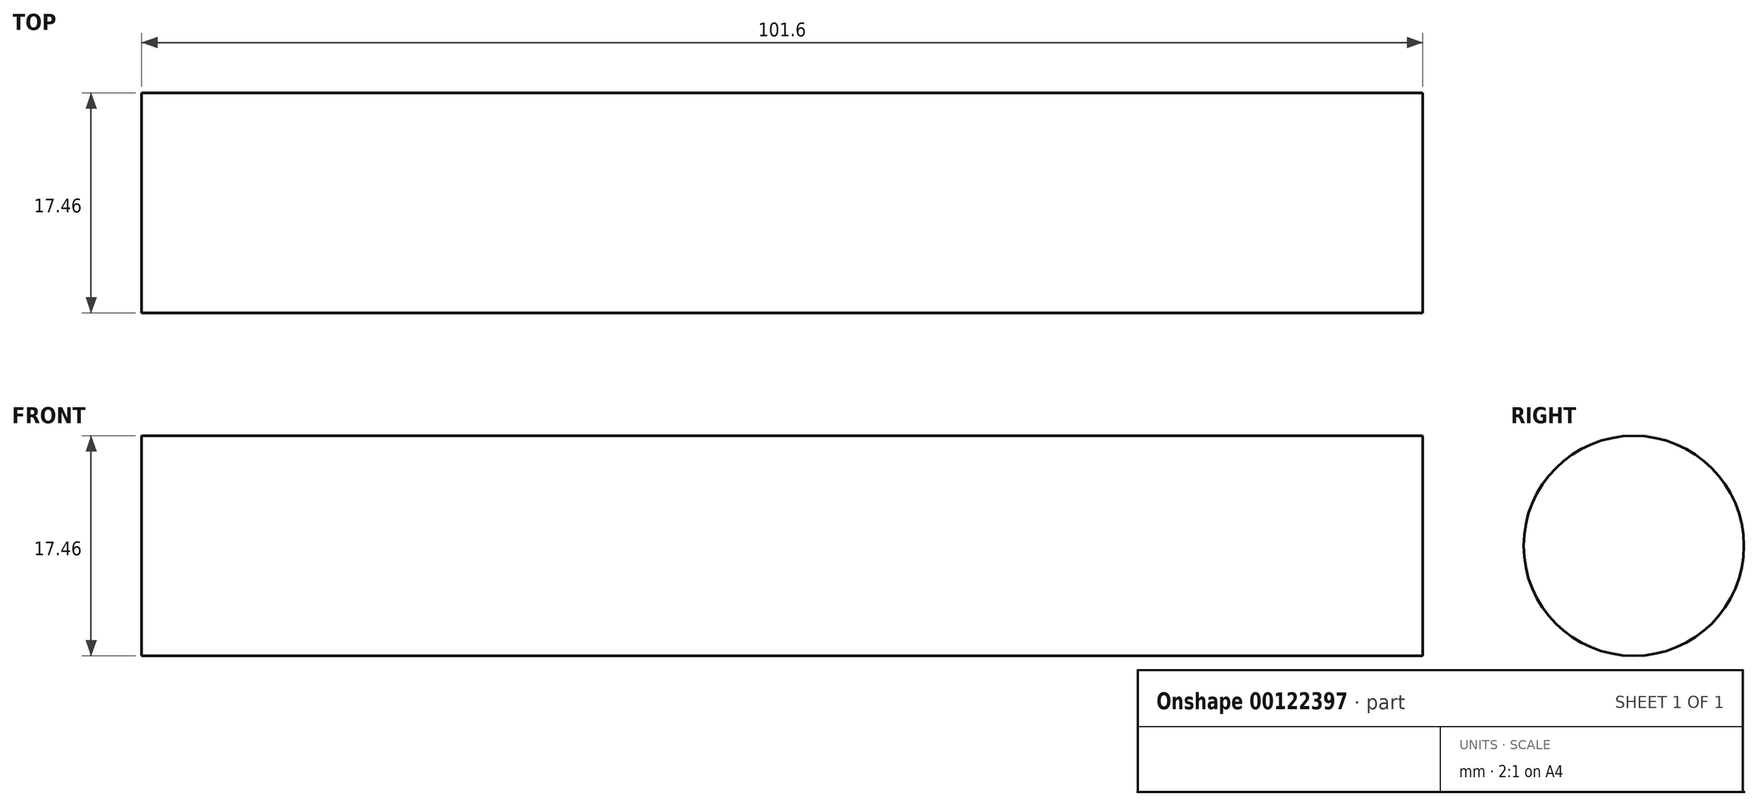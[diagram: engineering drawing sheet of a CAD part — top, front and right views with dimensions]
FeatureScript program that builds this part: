
annotation { "Feature Type Name" : "Feature", "Feature Type Description" : "" }
export const myFeature = defineFeature(function(context is Context, id is Id, definition is map)
    precondition{}
    {
        {
            var Q0;
            Q0=qCreatedBy(makeId("Right.planeOp"),FACE);
            var sketch = newSketch(context, id + "F0", { "sketchPlane" : qUnion([Q0])});
            skCircle(sketch, "E0", {"center": v(0, 0) * mm, "radius": 8.73 * mm});
            skSolve(sketch);
        }
        {
            var Q0;
            Q0=makeQuery(id+"F0.imprint","IMPRINT",FACE,{"disambiguationData":[TD([[makeQuery(id+"F0.imprint","IMPRINT",EDGE,{"derivedFrom":sQuery(id+"F0.wireOp",EDGE,"E0")}),1.0]])]});
            extrude(context, id + "F1", {"entities" : qUnion([Q0]), "depth" : 101.6 * mm});
        }
    });
